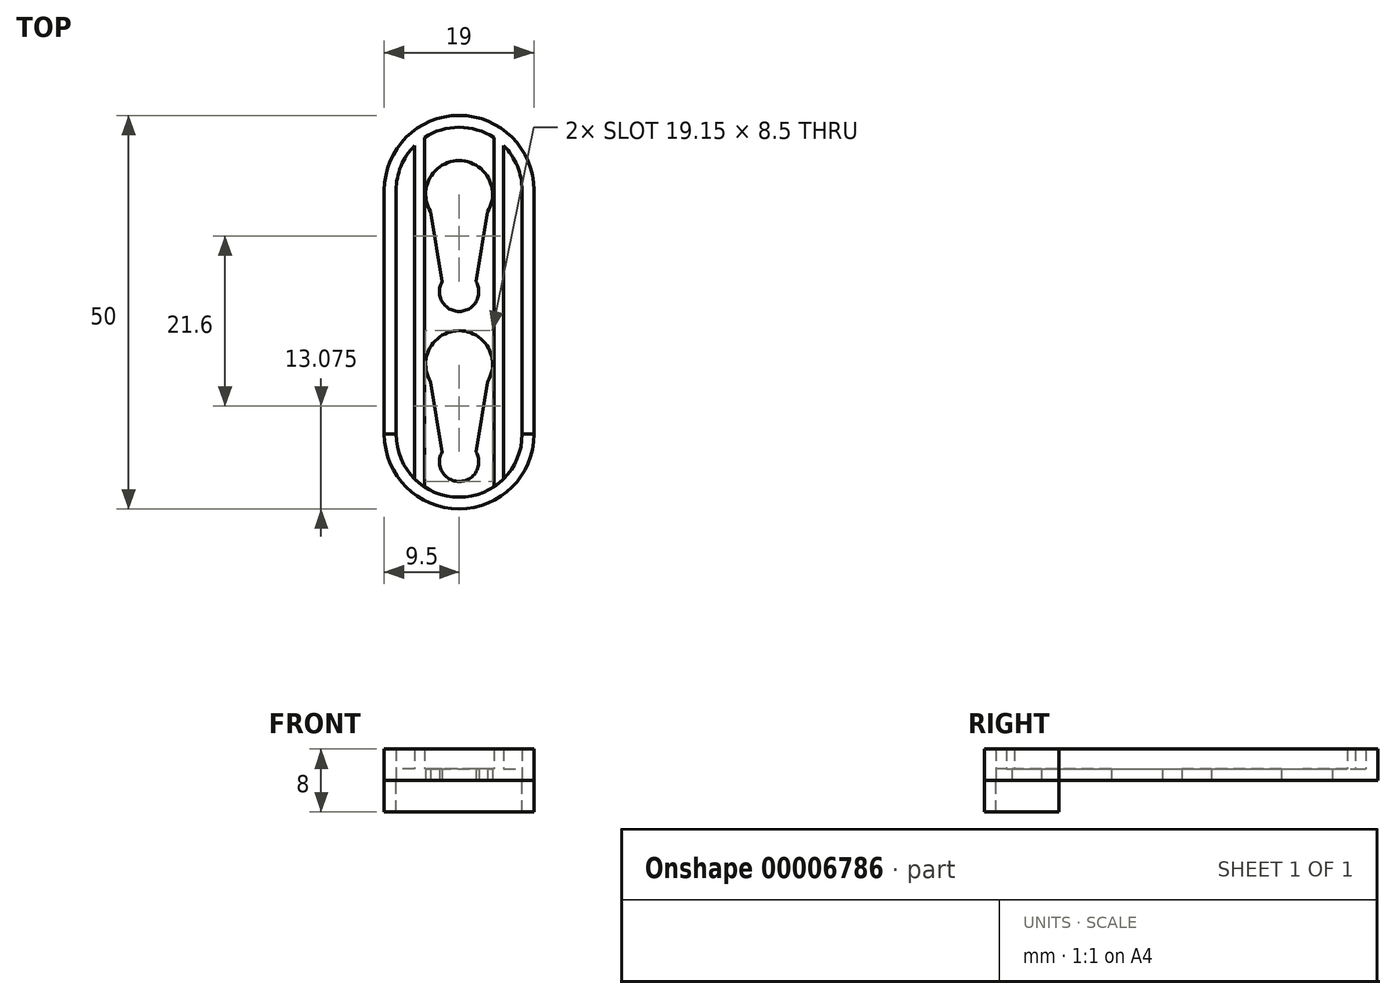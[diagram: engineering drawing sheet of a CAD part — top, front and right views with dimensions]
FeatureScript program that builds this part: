
annotation { "Feature Type Name" : "Feature", "Feature Type Description" : "" }
export const myFeature = defineFeature(function(context is Context, id is Id, definition is map)
    precondition{}
    {
        {
            var Q0;
            Q0=qCreatedBy(makeId("Top.planeOp"),FACE);
            var sketch = newSketch(context, id + "F0", { "sketchPlane" : qUnion([Q0])});
            skLineSegment(sketch, "E0.bottom", {"start": v(9.5, 0) * mm, "end": v(9.5, 0) * mm});
            skLineSegment(sketch, "E0.top", {"start": v(9.5, 50) * mm, "end": v(9.5, 50) * mm});
            skLineSegment(sketch, "E0.left", {"start": v(0, 9.5) * mm, "end": v(0, 40.5) * mm});
            skLineSegment(sketch, "E0.right", {"start": v(19, 9.5) * mm, "end": v(19, 40.5) * mm});
            skPoint(sketch, "E1.visualSharp", {"position": v(0, 50) * mm});
            skArc(sketch, "E1.filletArc", {"start": v(9.5, 50) * mm, "mid": v(2.78, 47.22) * mm, "end": v(0, 40.5) * mm});
            skPoint(sketch, "E2.visualSharp", {"position": v(0, 0) * mm});
            skArc(sketch, "E2.filletArc", {"start": v(0, 9.5) * mm, "mid": v(2.78, 2.78) * mm, "end": v(9.5, 0) * mm});
            skPoint(sketch, "E3.visualSharp", {"position": v(19, 0) * mm});
            skArc(sketch, "E3.filletArc", {"start": v(9.5, 0) * mm, "mid": v(16.22, 2.78) * mm, "end": v(19, 9.5) * mm});
            skPoint(sketch, "E4.visualSharp", {"position": v(19, 50) * mm});
            skArc(sketch, "E4.filletArc", {"start": v(19, 40.5) * mm, "mid": v(16.22, 47.22) * mm, "end": v(9.5, 50) * mm});
            skLineSegment(sketch, "E5", {"start": v(9.5, 50) * mm, "end": v(9.5, 44) * mm, "construction": true});
            skLineSegment(sketch, "E6", {"start": v(9.5, 44) * mm, "end": v(9.5, 40) * mm});
            skArc(sketch, "E7", {"start": v(13.11, 37.76) * mm, "mid": v(9.5, 44.25) * mm, "end": v(5.89, 37.76) * mm});
            skLineSegment(sketch, "E8", {"start": v(9.5, 40) * mm, "end": v(9.5, 18.4) * mm, "construction": true});
            skArc(sketch, "E9", {"start": v(13.11, 16.16) * mm, "mid": v(9.5, 22.65) * mm, "end": v(5.89, 16.16) * mm});
            skArc(sketch, "E10", {"start": v(7.35, 7.28) * mm, "mid": v(9.5, 3.5) * mm, "end": v(11.65, 7.28) * mm});
            skLineSegment(sketch, "E11", {"start": v(9.5, 0) * mm, "end": v(9.5, 6) * mm, "construction": true});
            skLineSegment(sketch, "E12", {"start": v(9.5, 18.4) * mm, "end": v(9.5, 6) * mm, "construction": true});
            skLineSegment(sketch, "E13", {"start": v(9.5, 40) * mm, "end": v(9.5, 27.6) * mm, "construction": true});
            skArc(sketch, "E14", {"start": v(7.35, 28.88) * mm, "mid": v(9.5, 25.1) * mm, "end": v(11.65, 28.88) * mm});
            skLineSegment(sketch, "E15", {"start": v(5.89, 37.76) * mm, "end": v(7.35, 28.88) * mm});
            skLineSegment(sketch, "E16.0.MirrorCS", {"start": v(13.11, 37.76) * mm, "end": v(11.65, 28.88) * mm});
            skLineSegment(sketch, "E17", {"start": v(5.89, 16.16) * mm, "end": v(7.35, 7.28) * mm});
            skLineSegment(sketch, "E18.0.MirrorCS", {"start": v(13.11, 16.16) * mm, "end": v(11.65, 7.28) * mm});
            skArc(sketch, "E19.0", {"start": v(9.5, 48.5) * mm, "mid": v(3.84, 46.16) * mm, "end": v(1.5, 40.5) * mm});
            skArc(sketch, "E19.1", {"start": v(17.5, 40.5) * mm, "mid": v(15.16, 46.16) * mm, "end": v(9.5, 48.5) * mm});
            skLineSegment(sketch, "E19.2", {"start": v(17.5, 9.5) * mm, "end": v(17.5, 40.5) * mm});
            skArc(sketch, "E19.3", {"start": v(9.5, 1.5) * mm, "mid": v(15.16, 3.84) * mm, "end": v(17.5, 9.5) * mm});
            skArc(sketch, "E19.4", {"start": v(1.5, 9.5) * mm, "mid": v(3.84, 3.84) * mm, "end": v(9.5, 1.5) * mm});
            skLineSegment(sketch, "E19.5", {"start": v(1.5, 9.5) * mm, "end": v(1.5, 40.5) * mm});
            skLineSegment(sketch, "E20", {"start": v(3.84, 3.84) * mm, "end": v(3.84, 46.16) * mm});
            skLineSegment(sketch, "E21", {"start": v(5.09, 2.83) * mm, "end": v(5.09, 47.17) * mm});
            skLineSegment(sketch, "E22.0.MirrorCS", {"start": v(13.91, 2.83) * mm, "end": v(13.91, 47.17) * mm});
            skLineSegment(sketch, "E23.0.MirrorCS", {"start": v(15.16, 3.84) * mm, "end": v(15.16, 46.16) * mm});
            skLineSegment(sketch, "E24", {"start": v(0, 9.5) * mm, "end": v(1.5, 9.5) * mm});
            skLineSegment(sketch, "E25", {"start": v(17.5, 9.5) * mm, "end": v(19, 9.5) * mm});
            skSolve(sketch);
        }
        {
            var Q0;
            Q0=makeQuery(id+"F0.imprint","IMPRINT",FACE,{"disambiguationData":[TD([[makeQuery(id+"F0.imprint","IMPRINT",EDGE,{"derivedFrom":sQuery(id+"F0.wireOp",EDGE,"E0.left")}),-1.0]])]});
            var Q1;
            {var subQ1=sQuery(id+"F0.wireOp",EDGE,"E20");Q1=makeQuery(id+"F0.imprint","IMPRINT",FACE,{"disambiguationData":[TD([[makeQuery(id+"F0.imprint","IMPRINT",EDGE,{"derivedFrom":subQ1}),-1.0]])]});}
            var Q2;
            {var subQ0=sQuery(id+"F0.wireOp",EDGE,"E22.0.MirrorCS");Q2=makeQuery(id+"F0.imprint","IMPRINT",FACE,{"disambiguationData":[TD([[makeQuery(id+"F0.imprint","IMPRINT",EDGE,{"derivedFrom":subQ0}),-1.0]])]});}
            extrude(context, id + "F1", {"entities" : qUnion([Q0, Q1, Q2]), "depth" : 4 * mm});
        }
        {
            var Q0;
            {var subQ1=sQuery(id+"F0.wireOp",EDGE,"E19.5");Q0=makeQuery(id+"F0.imprint","IMPRINT",FACE,{"disambiguationData":[TD([[makeQuery(id+"F0.imprint","IMPRINT",EDGE,{"derivedFrom":subQ1}),-1.0]])]});}
            var Q1;
            Q1=makeQuery(id+"F0.imprint","IMPRINT",FACE,{"disambiguationData":[TD([[makeQuery(id+"F0.imprint","IMPRINT",EDGE,{"derivedFrom":sQuery(id+"F0.wireOp",EDGE,"E9")}),-1.0]])]});
            var Q2;
            {var subQ2=sQuery(id+"F0.wireOp",EDGE,"E19.2");Q2=makeQuery(id+"F0.imprint","IMPRINT",FACE,{"disambiguationData":[TD([[makeQuery(id+"F0.imprint","IMPRINT",EDGE,{"derivedFrom":subQ2}),1.0]])]});}
            extrude(context, id + "F2", {"entities" : qUnion([Q0, Q1, Q2]), "operationType" : NewBodyOperationType.ADD, "depth" : 1.5 * mm});
        }
        {
            var Q0;
            Q0=makeQuery(id+"F0.imprint","IMPRINT",FACE,{"disambiguationData":[TD([[makeQuery(id+"F0.imprint","IMPRINT",EDGE,{"derivedFrom":sQuery(id+"F0.wireOp",EDGE,"E2.filletArc")}),1.0]])]});
            extrude(context, id + "F3", {"entities" : qUnion([Q0]), "operationType" : NewBodyOperationType.ADD, "oppositeDirection" : true, "depth" : 8 * mm});
        }
        {
            var Q0;
            Q0=makeQuery(id+"F0.imprint","IMPRINT",FACE,{"disambiguationData":[TD([[makeQuery(id+"F0.imprint","IMPRINT",EDGE,{"derivedFrom":sQuery(id+"F0.wireOp",EDGE,"E2.filletArc")}),1.0]])]});
            extrude(context, id + "F4", {"entities" : qUnion([Q0]), "depth" : 4 * mm});
        }
        {
            var Q0;
            Q0=makeQuery(id+"F3.opExtrude","CAP_FACE",FACE,{"disambiguationData":[OSD([sQuery(id+"F0.wireOp",EDGE,"E2.filletArc"),sQuery(id+"F0.wireOp",EDGE,"E3.filletArc"),sQuery(id+"F0.wireOp",EDGE,"E19.3"),sQuery(id+"F0.wireOp",EDGE,"E19.4"),sQuery(id+"F0.wireOp",EDGE,"E24"),sQuery(id+"F0.wireOp",EDGE,"E25")])],"isStart":false});
            extrude(context, id + "F5", {"entities" : qUnion([Q0]), "operationType" : NewBodyOperationType.REMOVE, "oppositeDirection" : true, "depth" : 4 * mm});
        }
    });
